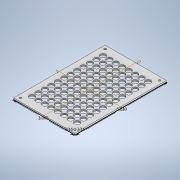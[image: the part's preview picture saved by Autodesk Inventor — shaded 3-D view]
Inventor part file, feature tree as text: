
AUTODESK INVENTOR PART (.ipt)
format: ipt  version: 2020 (Build 240168000, 168)  size: 271,872 bytes
history: native  units: in
note: dims shown in document units (in); Inventor stores cm internally (conversion verified against a paired STEP export)
features: sketch x2, hole x2, plane x2, mirror x2, extrude x1, pattern_linear x1
ambient origin geometry x8: Origin, YZ Plane, XZ Plane, XY Plane, X Axis, Y Axis, Z Axis, Center Point
bodies: Solid1 (feature_tree)
feature tree (10):
  sketch  "Sketch1"  dims[d0=3.365in d1=5.03in]
  extrude  "Extrusion1"  Depth=5.03in
  hole  "Hole1"  [1 undecoded]
  pattern_linear  "Rectangular Pattern1"  Spacing1=0.5661in  [1 undecoded]
  plane  "Work Plane1"
  plane  "Work Plane2"
  hole  "Hole2"  [1 undecoded]
  mirror  "Mirror1"
  mirror  "Mirror2"
  sketch  "Sketch2"  dims[d2=0.0787in d3=0.0in d4=0.4425in d5=0.5661in d6=0.2756in d7=0.2953in d8=0.75in d9=0.37in d10=0.25in d11=90.0deg d12=0.75in d13=0.0in d14=3.1496in d16=0.3543in d17=4.7244in d19=0.3543in d20=0.1875in d21=0.1875in d22=0.1181in d23=0.75in d24=0.375in d25=0.25in d26=0.5635in d27=1.0in d28=0.8108in d29=1.0in d30=1.0in d31=1.0in d32=0.15in d33=0.25in d34=0.375in d35=0.5635in d36=0.75in d37=0.8108in d38=0.0625in d39=0.75in d40=0.375in]
note: 3 required parameter values undecoded (feature->parameter linkage not recoverable at this tier; creation-order binding heuristic only, values carry confidence <= 0.55)
